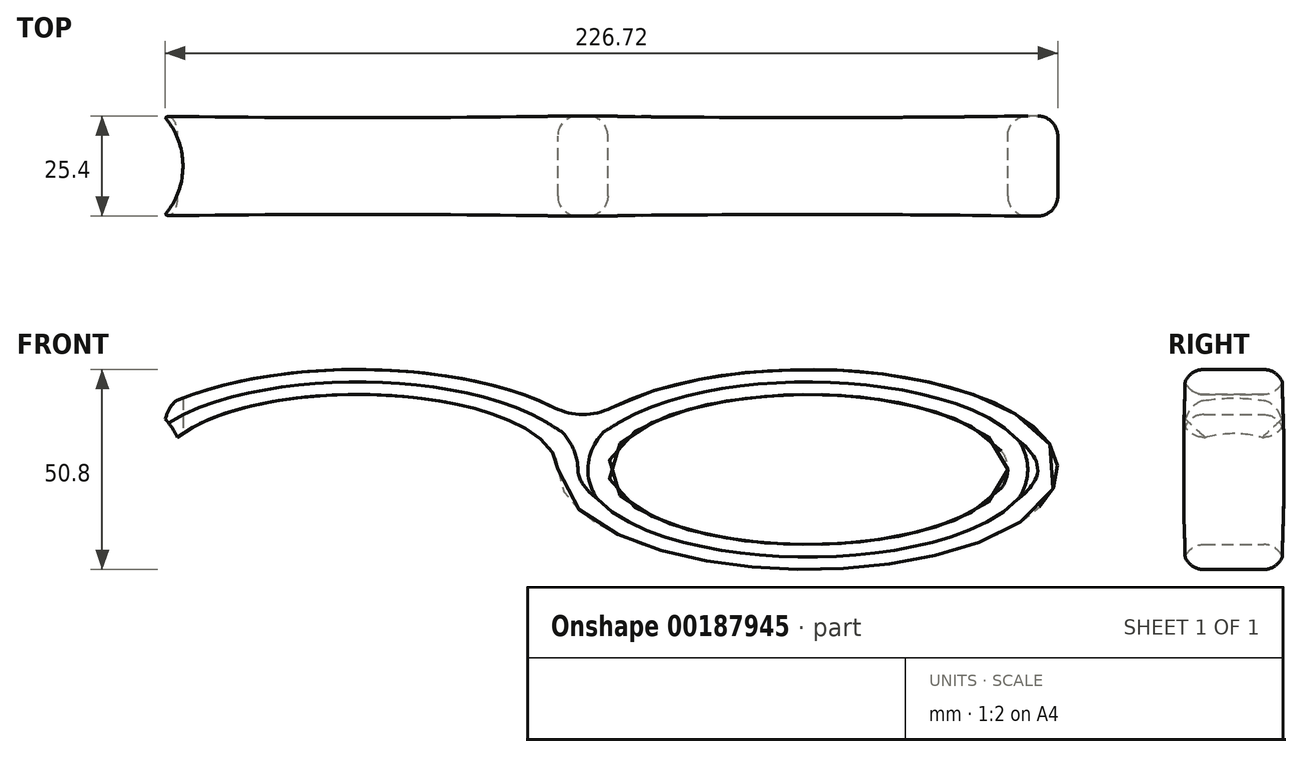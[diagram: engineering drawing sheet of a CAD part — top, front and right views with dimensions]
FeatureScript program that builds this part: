
annotation { "Feature Type Name" : "Feature", "Feature Type Description" : "" }
export const myFeature = defineFeature(function(context is Context, id is Id, definition is map)
    precondition{}
    {
        {
            var Q0;
            Q0=qCreatedBy(makeId("Front.planeOp"),FACE);
            var sketch = newSketch(context, id + "F0", { "sketchPlane" : qUnion([Q0])});
            skEllipticalArc(sketch, "E0", {});
            skEllipticalArc(sketch, "E1", {});
            skEllipse(sketch, "E2", {"center": v(114.3, 32.66) * mm, "majorRadius": 50.8 * mm, "minorRadius": 19.05 * mm, "majorAxis": v(1, 0)});
            skEllipticalArc(sketch, "E3", {});
            skLineSegment(sketch, "E4", {"start": v(-63.5, 32.66) * mm, "end": v(-50.8, 32.66) * mm});
            const initialGuessF0  = {"E0": [0, 0.032663216814398766, 1, 0, 0.0508, 0.01905, 0, 3.141592653589793], "E1": [0, 0.032663216814398766, 1, 0, 0.0635, 0.0254, 0.4510268117962622, 3.141592653589793], "E3": [0.1143, 0.032663216814398766, 1, 0, 0.0635, 0.0254, 3.141592653589793, 2.6905658417935308]};
            skSetInitialGuess(sketch, initialGuessF0);
            skSolve(sketch);
        }
        {
            var Q0;
            Q0=makeQuery(id+"F0.imprint","IMPRINT",FACE,{"disambiguationData":[TD([[makeQuery(id+"F0.imprint","IMPRINT",EDGE,{"derivedFrom":sQuery(id+"F0.wireOp",EDGE,"E0")}),-1.0]])]});
            extrude(context, id + "F1", {"entities" : qUnion([Q0]), "endBound" : BoundingType.SYMMETRIC, "depth" : 25.4 * mm});
        }
        {
            var Q0;
            Q0=makeQuery(id+"F1.opExtrude","SWEPT_EDGE",EDGE,{"disambiguationData":[OSD([sQuery(id+"F0.wireOp",EDGE,"E1"),sQuery(id+"F0.wireOp",EDGE,"E3")])]});
            fillet(context, id + "F2", {"entities" : qUnion([Q0]), "radius" : 15.88 * mm, "tangentPropagation" : true, "allowEdgeOverflow" : false});
        }
        {
            var Q0;
            Q0=makeQuery(id+"F1.opExtrude","SWEPT_FACE",FACE,{"disambiguationData":[OSD([sQuery(id+"F0.wireOp",EDGE,"E4")])]});
            var sketch = newSketch(context, id + "F3", { "sketchPlane" : qUnion([Q0])});
            skLineSegment(sketch, "E5", {"start": v(-50.8, 0) * mm, "end": v(-110.9, 0) * mm});
            skPoint(sketch, "E5.endSnap0", {"position": v(-50.8, 0) * mm});
            skCircle(sketch, "E6", {"center": v(-110.9, 0) * mm, "radius": 60.1 * mm});
            skLineSegment(sketch, "E7", {"start": v(-50.8, -12.7) * mm, "end": v(-50.8, 12.7) * mm});
            skLineSegment(sketch, "E8", {"start": v(50.8, 12.7) * mm, "end": v(50.8, -12.7) * mm});
            skSolve(sketch);
        }
        {
            var Q0;
            {var subQ0=sQuery(id+"F0.wireOp",EDGE,"E4");var subQ4=sQuery(id+"F3.wireOp",EDGE,"E6");var subQ6=makeQuery(id+"F1.opExtrude","CAP_EDGE",EDGE,{"disambiguationData":[OSD([subQ0])],"isStart":false});var subQ9=makeQuery(id+"F3.imprint","INTERSECT",VERTEX,{"derivedFrom":[subQ6,subQ4]});Q0=makeQuery(id+"F3.imprint","IMPRINT",FACE,{"disambiguationData":[TD([[makeQuery(id+"F3.imprint","IMPRINT",EDGE,{"disambiguationData":[TD([[subQ9,-1.0]])],"derivedFrom":subQ4}),1.0]])]});}
            extrude(context, id + "F4", {"entities" : qUnion([Q0]), "oppositeDirection" : true, "depth" : 25.4 * mm});
        }
        {
            var Q0;
            Q0=makeQuery(id+"F4.opExtrude","SWEPT_BODY",BODY,{"disambiguationData":[OSD([sQuery(id+"F0.wireOp",EDGE,"E1"),sQuery(id+"F0.wireOp",EDGE,"E4"),sQuery(id+"F3.wireOp",EDGE,"E6")])]});
            deleteBodies(context, id + "F5", {"entities" : qUnion([Q0])});
        }
        {
            var Q0;
            Q0=qCreatedBy(makeId("Front.planeOp"),FACE);
            var sketch = newSketch(context, id + "F6", { "sketchPlane" : qUnion([Q0])});
            skCircle(sketch, "E9", {"center": v(-63.16, 32.8) * mm, "radius": 19.05 * mm});
            skSolve(sketch);
        }
        {
            var Q0;
            Q0=makeQuery(id+"F6.imprint","IMPRINT",FACE,{"disambiguationData":[TD([[makeQuery(id+"F6.imprint","IMPRINT",EDGE,{"derivedFrom":sQuery(id+"F6.wireOp",EDGE,"E9")}),1.0]])]});
            extrude(context, id + "F7", {"entities" : qUnion([Q0]), "operationType" : NewBodyOperationType.REMOVE, "endBound" : BoundingType.SYMMETRIC, "oppositeDirection" : true, "depth" : 25.4 * mm});
        }
        {
            var Q0;
            Q0=makeQuery(id+"F1.opExtrude","CAP_EDGE",EDGE,{"disambiguationData":[OSD([sQuery(id+"F0.wireOp",EDGE,"E3")])],"isStart":false});
            var Q1;
            Q1=makeQuery(id+"F1.opExtrude","CAP_EDGE",EDGE,{"disambiguationData":[OSD([sQuery(id+"F0.wireOp",EDGE,"E3")])],"isStart":true});
            var Q2;
            Q2=makeQuery(id+"F1.opExtrude","SWEPT_FACE",FACE,{"disambiguationData":[OSD([sQuery(id+"F0.wireOp",EDGE,"E2")])]});
            fillet(context, id + "F8", {"entities" : qUnion([Q0, Q1, Q2]), "radius" : 5.08 * mm, "tangentPropagation" : true, "allowEdgeOverflow" : false});
        }
        {
            var Q0;
            Q0=qCreatedBy(makeId("Top.planeOp"),FACE);
            var sketch = newSketch(context, id + "F9", { "sketchPlane" : qUnion([Q0])});
            skLineSegment(sketch, "E10", {"start": v(-21.02, 0) * mm, "end": v(-66.55, 0) * mm, "construction": true});
            skCircle(sketch, "E11", {"center": v(-63.5, 0) * mm, "radius": 19.05 * mm});
            skSolve(sketch);
        }
        {
            var Q0;
            Q0=makeQuery(id+"F9.imprint","IMPRINT",FACE,{"disambiguationData":[TD([[makeQuery(id+"F9.imprint","IMPRINT",EDGE,{"derivedFrom":sQuery(id+"F9.wireOp",EDGE,"E11")}),1.0]])]});
            extrude(context, id + "F10", {"entities" : qUnion([Q0]), "operationType" : NewBodyOperationType.REMOVE, "endBound" : BoundingType.THROUGH_ALL, "depth" : 25.4 * mm});
        }
    });
